# Revit family: Door - Double - Barn Swinging - P - WH
name_source: partatom
category: Doors
units: mm (PartAtom-declared; Revit-internal decimal feet)

## family parameters
Always vertical = Yes
Cut with Voids When Loaded = No
Host = Wall
OmniClass Number = 23.30.10.00
OmniClass Title = Doors
Room Calculation Point = No
Shared = No

## types (1)
- Double - Barn Swinging
    Analytic Construction = <None>
    Define Thermal Properties by = Schematic Type
    Door Panel = <By Category>
    Door Panel Framing = <By Category>
    Door Panel Thickness = 19 mm  [stored 0.062336 ft]
    Door Width = 900 mm  [stored 2.95276 ft]
    Frame = <By Category>
    Frame Thickness = 19 mm  [stored 0.062336 ft]
    Frame Width = 100 mm  [stored 0.328084 ft]
    Function = Interior
    Height = 2150 mm
    Hinge = <By Category>
    Hinge Height = 160 mm  [stored 0.524934 ft]
    Hinge Length = 300 mm
    Hinge Width = 50 mm  [stored 0.164042 ft]
    Panel Framing Depth = 38 mm  [stored 0.124672 ft]
    Panel Framing Width = 89 mm  [stored 0.291995 ft]
    Thickness = 57 mm
    Wall Closure = By host
    Width = 1800 mm  [stored 5.90551 ft]

note: [stored X ft] marks values corroborated as IEEE doubles in the binary element streams (Revit-internal decimal feet)

## geometry (parser evidence)
native form markers: Sweep x5
no freeform markers — native parametric forms only
